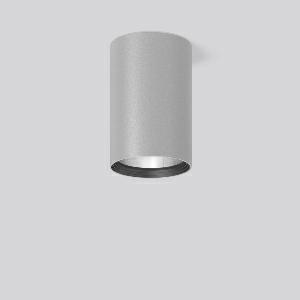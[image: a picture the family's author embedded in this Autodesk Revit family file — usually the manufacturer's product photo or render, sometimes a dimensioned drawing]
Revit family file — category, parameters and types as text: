
# Revit family: heledon_maxi_a_931216_004_1_ed88
name_source: partatom
category: Lighting Fixtures
units: mm (PartAtom-declared; Revit-internal decimal feet)

## family parameters
Cut with Voids When Loaded = No
Host = Face
Light Source = No
Part Type = Normal
Room Calculation Point = No
Round Connector Dimension = Use Diameter
Shared = No

## types (1)
- HELEDON maxi A (1 x LED Modul 940, 3400 lm, 4000)
    Apparent Load = 25 VA
    Approval mark = CE
    CIE Flux Codes = 100 100 100 100 100
    Color Rendering = 92
    Color Temperature = 4000
    Default Elevation = 1800 mm
    Description = Series: HELEDON maxi
Cylindrical surface-mounted downlight. Housing: die-cast aluminium, powder-coated. Internal ceiling frame polycarbonate with bayonet mounting. Black plastic ring and recessed LED to prevent glare from the side. Optical assembly with reflector made of MIRO-Silver with 98% total light reflection for outstanding efficiency - can be changed without tools. Best colour rendering index Ra>90. Suitable for Ceiling mounting. Easy installation with a separate ceiling frame with bayonet mounting and plug connection. Driver integrated. Connected via plug-in connector. High quality converter without flickering and stroboscopic effect. The following accessories can be mounted without use of tools: interchangeable lenses, decorative glasses, honeycomb louvre, clear and frosted diffusers, white interchangeable plastic ring. 
Colour: silver
Diameter: 123 mm
Height: 183 mm
Lamp: LED
Socket: without socket
Colour temperature: 4000K
Colour rendering index (CRI): 92
System power: 25 W
Rated luminous flux: 3400 lm
Luminous efficiency: 136 lm/W
Control gear: Regulated power supply
Protection class: I
Type of protection: IP 20
    Height = 183 mm
    Lamp = 1 x LED Modul 940
    Lamp Light Flux = 3400 lm
    Lamp count = 1
    Length = 123 mm
    Lifetime = 50000 h
    Luminous efficacy = 136 lm/W
    Manufacturer = RZB
    ModVariant = No
    Model = 931216.004.1
    Mounting Place = Ceiling
    Mounting Type = Surface mounted
    Number of Poles = 1
    OnlyDefault = Yes
    Power Factor = 1
    Product Name = HELEDON maxi A
    Product group = Surface mounted downlights
    ProductGroupID = 302
    Protection Class = Protection class I
    Protection Degree = IP 20
    RLX_Detail_Level = 1
    RLX_Emergency_Light_Flux = 0 lm
    RLX_Emergency_Type = 0
    RLX_Emergency_Type_DB = No
    RlxData = <blob elided: 98625 chars, md5=0a235066>
    Socket = socket
    Standby Power = 0 W
    System Light Flux = 3400 lm
    System Power = 25 W
    Type Comments = Product without accessories
    Type Image = 931192.004.jpg
    URL = http://relux.com
    VarID = ---
    Voltage = 230 V
    Voltage Range = 220-240 V
    Weight = 0.00 kg
    Width = 0 mm  [stored 0 ft]

note: [stored X ft] marks values corroborated as IEEE doubles in the binary element streams (Revit-internal decimal feet)

## geometry (parser evidence)
native form markers: Blend x4, Sweep x11
no freeform markers — native parametric forms only
